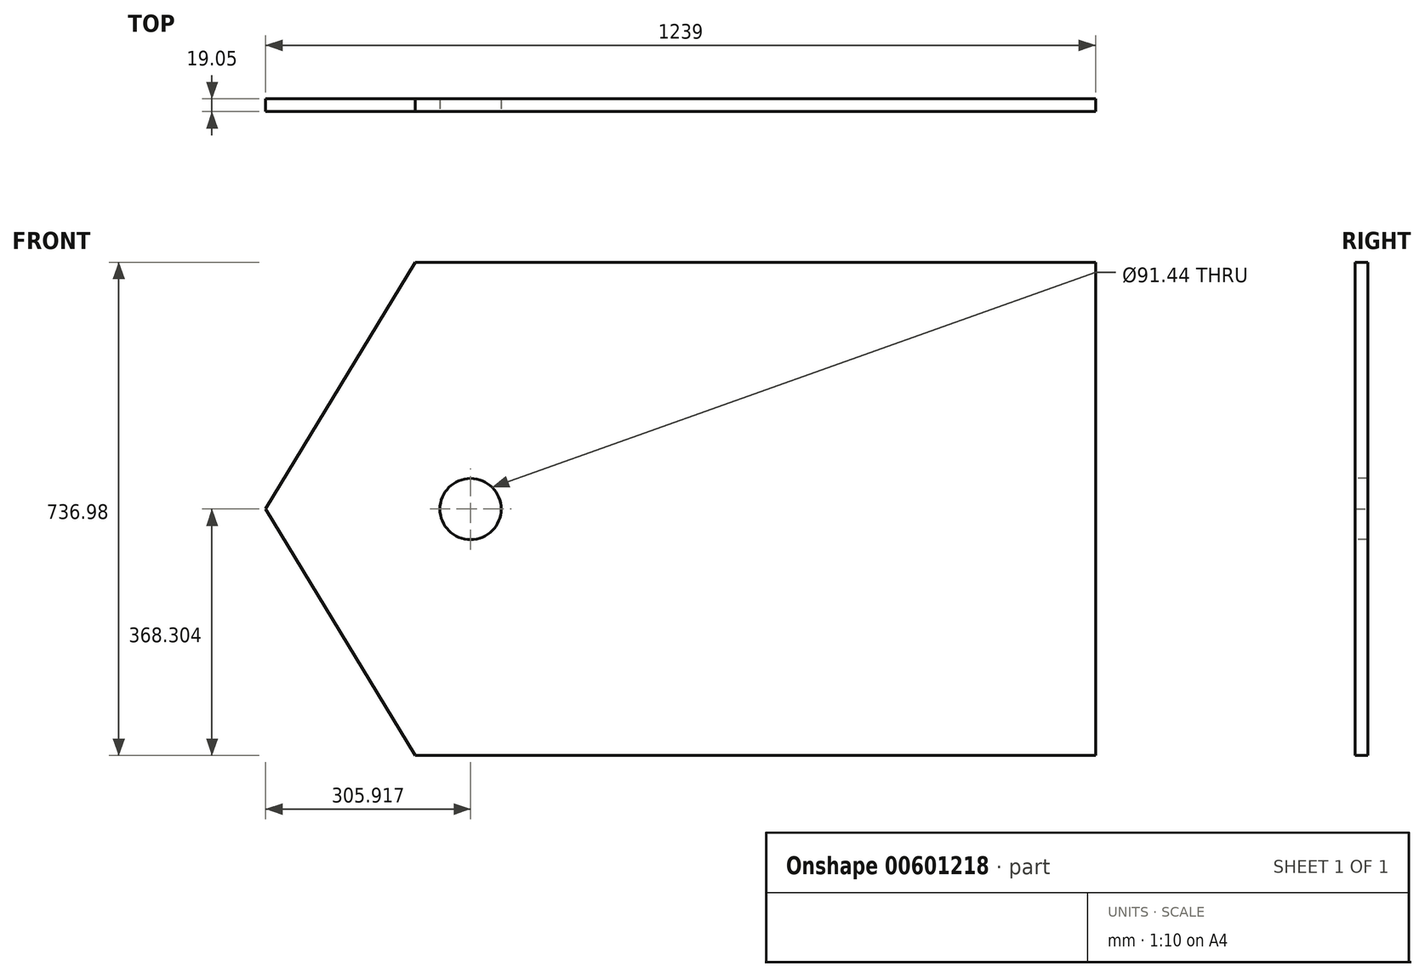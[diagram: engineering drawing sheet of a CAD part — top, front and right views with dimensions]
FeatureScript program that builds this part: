
annotation { "Feature Type Name" : "Feature", "Feature Type Description" : "" }
export const myFeature = defineFeature(function(context is Context, id is Id, definition is map)
    precondition{}
    {
        {
            var Q0;
            Q0=qCreatedBy(makeId("Front.planeOp"),FACE);
            var sketch = newSketch(context, id + "F0", { "sketchPlane" : qUnion([Q0])});
            skLineSegment(sketch, "E0", {"start": v(-913.43, -81.79) * mm, "end": v(-690.08, -450.09) * mm});
            skLineSegment(sketch, "E1", {"start": v(-690.08, 286.51) * mm, "end": v(-913.43, -81.79) * mm});
            skLineSegment(sketch, "E2", {"start": v(325.57, 286.89) * mm, "end": v(198.57, 286.89) * mm});
            skLineSegment(sketch, "E3", {"start": v(-563.7, -449.71) * mm, "end": v(198.3, -449.71) * mm});
            skLineSegment(sketch, "E4", {"start": v(-563.7, 286.89) * mm, "end": v(198.3, 286.89) * mm});
            skLineSegment(sketch, "E5", {"start": v(198.3, -449.71) * mm, "end": v(325.57, -449.71) * mm});
            skLineSegment(sketch, "E6", {"start": v(-690.08, -450.09) * mm, "end": v(-563.7, -449.71) * mm});
            skLineSegment(sketch, "E7", {"start": v(-690.08, 286.51) * mm, "end": v(-563.7, 286.89) * mm});
            skLineSegment(sketch, "E8", {"start": v(325.57, -449.71) * mm, "end": v(325.57, 286.89) * mm});
            skLineSegment(sketch, "E9.bottom", {"start": v(-690.08, -450.09) * mm, "end": v(325.57, -450.09) * mm});
            skLineSegment(sketch, "E9.top", {"start": v(-690.08, 286.89) * mm, "end": v(325.57, 286.89) * mm});
            skLineSegment(sketch, "E9.left", {"start": v(-690.08, 286.51) * mm, "end": v(-690.08, 286.89) * mm});
            skLineSegment(sketch, "E9.right", {"start": v(325.57, -450.09) * mm, "end": v(325.57, 286.89) * mm});
            skSolve(sketch);
        }
        {
            var Q0;
            Q0 = qSketchRegion(id + "F0", true);
            extrude(context, id + "F1", {"entities" : qUnion([Q0]), "depth" : 19.05 * mm, "offsetDistance" : 25.4 * mm});
        }
        {
            var Q0;
            Q0=makeQuery(id+"F1.opExtrude","CAP_FACE",FACE,{"disambiguationData":[OSD([sQuery(id+"F0.wireOp",EDGE,"E0"),sQuery(id+"F0.wireOp",EDGE,"E1"),sQuery(id+"F0.wireOp",EDGE,"E9.bottom"),sQuery(id+"F0.wireOp",EDGE,"E9.top"),sQuery(id+"F0.wireOp",EDGE,"E9.left"),sQuery(id+"F0.wireOp",EDGE,"E9.right")])],"isStart":false});
            var sketch = newSketch(context, id + "F2", { "sketchPlane" : qUnion([Q0])});
            skCircle(sketch, "E10", {"center": v(-607.51, -81.79) * mm, "radius": 45.72 * mm});
            skSolve(sketch);
        }
        {
            var Q0;
            Q0 = qSketchRegion(id + "F2", true);
            extrude(context, id + "F3", {"entities" : qUnion([Q0]), "operationType" : NewBodyOperationType.REMOVE, "oppositeDirection" : true, "depth" : 25.4 * mm, "offsetDistance" : 25.4 * mm});
        }
    });
